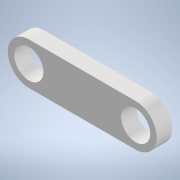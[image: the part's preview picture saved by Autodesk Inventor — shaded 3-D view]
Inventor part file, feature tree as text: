
AUTODESK INVENTOR PART (.ipt)
format: ipt  version: 2020 (Build 240168000, 168)  size: 112,640 bytes
history: native  units: in
note: dims shown in document units (in); Inventor stores cm internally (conversion verified against a paired STEP export)
features: extrude x2, sketch x2
ambient origin geometry x8: Origin, YZ Plane, XZ Plane, XY Plane, X Axis, Y Axis, Z Axis, Center Point
bodies: Solid1 (feature_tree)
feature tree (4):
  extrude  "Extrusion1"  Depth=0.813in
  extrude  "Extrusion2"  Depth=0.6in
  sketch  "Sketch1"  dims[d0=4.125in d1=0.813in]
  sketch  "Sketch2"  dims[d2=0.6in d3=0.0in d4=1.126in d5=0.0in d6=0.0in]
